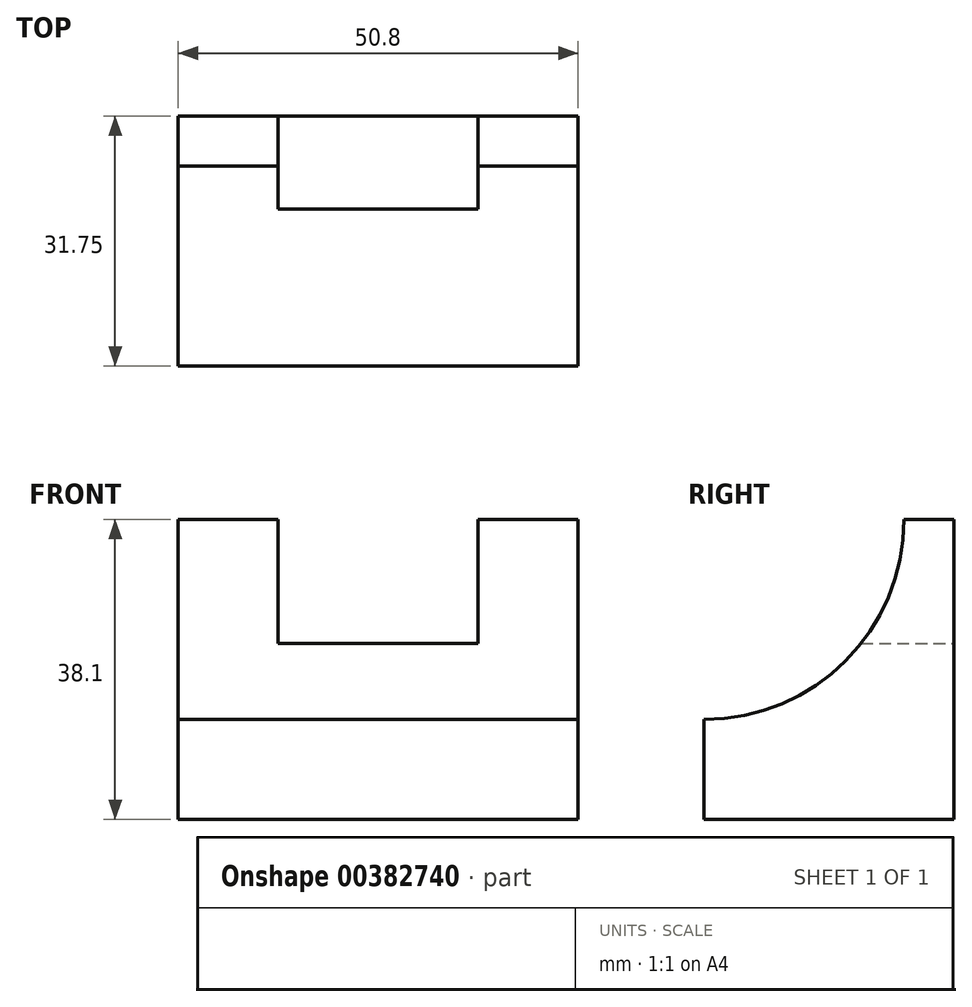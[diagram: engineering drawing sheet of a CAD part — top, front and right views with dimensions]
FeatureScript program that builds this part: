
annotation { "Feature Type Name" : "Feature", "Feature Type Description" : "" }
export const myFeature = defineFeature(function(context is Context, id is Id, definition is map)
    precondition{}
    {
        {
            var Q0;
            Q0=qCreatedBy(makeId("Front.planeOp"),FACE);
            var sketch = newSketch(context, id + "F0", { "sketchPlane" : qUnion([Q0])});
            skLineSegment(sketch, "E0", {"start": v(0, 0) * mm, "end": v(0, 38.1) * mm});
            skLineSegment(sketch, "E1", {"start": v(0, 38.1) * mm, "end": v(-12.7, 38.1) * mm});
            skLineSegment(sketch, "E2", {"start": v(-12.7, 38.1) * mm, "end": v(-12.7, 22.38) * mm});
            skLineSegment(sketch, "E3", {"start": v(-12.7, 22.38) * mm, "end": v(-38.1, 22.38) * mm});
            skLineSegment(sketch, "E4", {"start": v(-38.1, 22.38) * mm, "end": v(-38.1, 38.1) * mm});
            skLineSegment(sketch, "E5", {"start": v(-38.1, 38.1) * mm, "end": v(-50.8, 38.1) * mm});
            skLineSegment(sketch, "E6", {"start": v(-50.8, 38.1) * mm, "end": v(-50.8, 0) * mm});
            skLineSegment(sketch, "E7", {"start": v(-50.8, 0) * mm, "end": v(0, 0) * mm});
            skSolve(sketch);
        }
        {
            var Q0;
            Q0=makeQuery(id+"F0.imprint","IMPRINT",FACE,{"disambiguationData":[TD([[makeQuery(id+"F0.imprint","IMPRINT",EDGE,{"derivedFrom":sQuery(id+"F0.wireOp",EDGE,"E0")}),1.0]])]});
            extrude(context, id + "F1", {"entities" : qUnion([Q0]), "depth" : 31.75 * mm});
        }
        {
            var Q0;
            Q0=makeQuery(id+"F1.opExtrude","SWEPT_FACE",FACE,{"disambiguationData":[OSD([sQuery(id+"F0.wireOp",EDGE,"E0")])]});
            var sketch = newSketch(context, id + "F2", { "sketchPlane" : qUnion([Q0])});
            skArc(sketch, "E8", {"start": v(-31.75, 12.7) * mm, "mid": v(-13.79, 20.14) * mm, "end": v(-6.35, 38.1) * mm});
            skSolve(sketch);
        }
        {
            var Q0;
            {var subQ0=sQuery(id+"F2.wireOp",EDGE,"E8");Q0=makeQuery(id+"F2.imprint","IMPRINT",FACE,{"disambiguationData":[TD([[makeQuery(id+"F2.imprint","IMPRINT",EDGE,{"derivedFrom":subQ0}),1.0]])]});}
            extrude(context, id + "F3", {"entities" : qUnion([Q0]), "operationType" : NewBodyOperationType.REMOVE, "oppositeDirection" : true, "depth" : 50.8 * mm});
        }
    });
